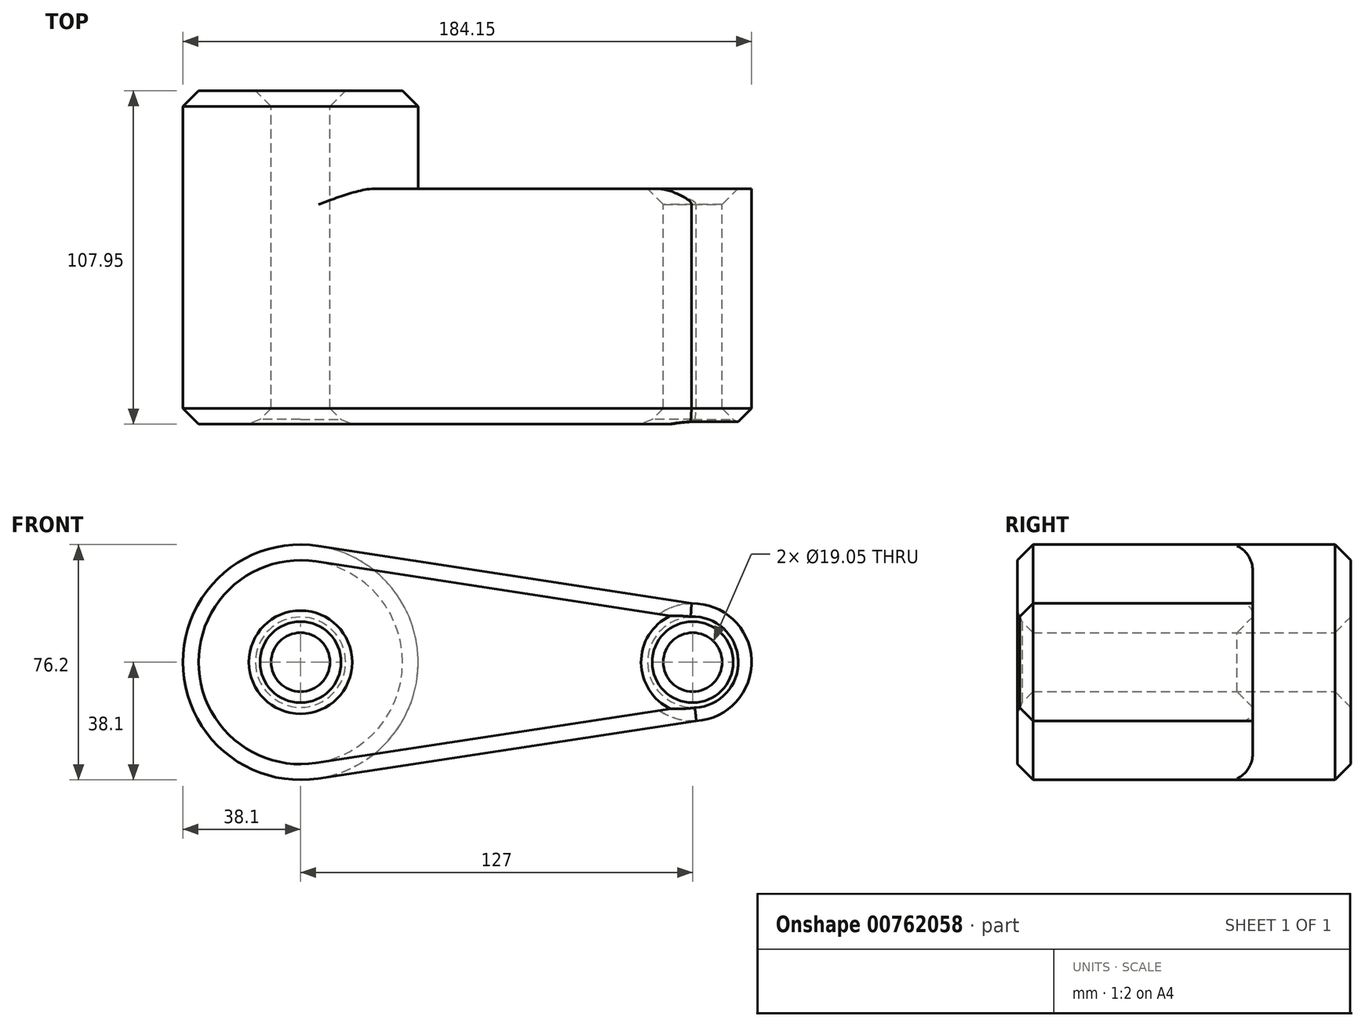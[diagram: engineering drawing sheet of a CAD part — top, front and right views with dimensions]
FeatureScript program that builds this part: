
annotation { "Feature Type Name" : "Feature", "Feature Type Description" : "" }
export const myFeature = defineFeature(function(context is Context, id is Id, definition is map)
    precondition{}
    {
        {
            var Q0;
            Q0=qCreatedBy(makeId("Front.planeOp"),FACE);
            var sketch = newSketch(context, id + "F0", { "sketchPlane" : qUnion([Q0])});
            skCircle(sketch, "E0", {"center": v(0, 0) * mm, "radius": 38.1 * mm});
            skCircle(sketch, "E1", {"center": v(127, 0) * mm, "radius": 19.05 * mm});
            skLineSegment(sketch, "E2", {"start": v(5.8, 37.66) * mm, "end": v(126.63, 19.05) * mm});
            skLineSegment(sketch, "E3", {"start": v(5.74, -37.67) * mm, "end": v(131.55, -18.5) * mm});
            skCircle(sketch, "E4", {"center": v(0, 0) * mm, "radius": 9.53 * mm});
            skCircle(sketch, "E5", {"center": v(127, 0) * mm, "radius": 9.53 * mm});
            skSolve(sketch);
        }
        {
            var Q0;
            Q0 = qSketchRegion(id + "F0", true);
            extrude(context, id + "F1", {"entities" : qUnion([Q0]), "depth" : 76.2 * mm, "offsetDistance" : 25.4 * mm});
        }
        {
            var Q0;
            Q0=makeQuery(id+"F0.imprint","IMPRINT",FACE,{"disambiguationData":[TD([[makeQuery(id+"F0.imprint","IMPRINT",EDGE,{"derivedFrom":sQuery(id+"F0.wireOp",EDGE,"E4")}),-1.0]])]});
            extrude(context, id + "F2", {"entities" : qUnion([Q0]), "operationType" : NewBodyOperationType.ADD, "oppositeDirection" : true, "depth" : 31.75 * mm, "offsetDistance" : 25.4 * mm});
        }
        {
            var Q0;
            Q0=makeQuery(id+"F2.opExtrude","CAP_EDGE",EDGE,{"disambiguationData":[OSD([sQuery(id+"F0.wireOp",EDGE,"E4")])],"isStart":false});
            chamfer(context, id + "F3", {"entities" : qUnion([Q0]), "chamferType" : ChamferType.OFFSET_ANGLE, "width" : 5.08 * mm, "oppositeDirection" : false, "angle" : 45 * degree, "tangentPropagation" : true});
        }
        {
            var Q0;
            Q0=makeQuery(id+"F2.opExtrude","CAP_EDGE",EDGE,{"disambiguationData":[OSD([sQuery(id+"F0.wireOp",EDGE,"E0")])],"isStart":false});
            chamfer(context, id + "F4", {"entities" : qUnion([Q0]), "width" : 5.08 * mm, "tangentPropagation" : true});
        }
        {
            var Q0;
            Q0=makeQuery(id+"F1.opExtrude","CAP_EDGE",EDGE,{"disambiguationData":[OSD([sQuery(id+"F0.wireOp",EDGE,"E5")])],"isStart":true});
            chamfer(context, id + "F5", {"entities" : qUnion([Q0]), "width" : 5.08 * mm, "tangentPropagation" : true});
        }
        {
            var Q0;
            Q0=makeQuery(id+"F1.opExtrude","CAP_EDGE",EDGE,{"disambiguationData":[OSD([sQuery(id+"F0.wireOp",EDGE,"E4")])],"isStart":false});
            var Q1;
            Q1=makeQuery(id+"F1.opExtrude","CAP_EDGE",EDGE,{"disambiguationData":[OSD([sQuery(id+"F0.wireOp",EDGE,"E5")])],"isStart":false});
            chamfer(context, id + "F6", {"entities" : qUnion([Q0, Q1]), "width" : 5.08 * mm, "tangentPropagation" : true});
        }
        {
            var Q0;
            Q0=makeQuery(id+"F1.opExtrude","CAP_FACE",FACE,{"disambiguationData":[OSD([sQuery(id+"F0.wireOp",EDGE,"E0"),sQuery(id+"F0.wireOp",EDGE,"E1"),sQuery(id+"F0.wireOp",EDGE,"E2"),sQuery(id+"F0.wireOp",EDGE,"E3"),sQuery(id+"F0.wireOp",EDGE,"E4"),sQuery(id+"F0.wireOp",EDGE,"E5")])],"isStart":false});
            chamfer(context, id + "F7", {"entities" : qUnion([Q0]), "width" : 5.08 * mm, "tangentPropagation" : true});
        }
        {
            var Q0;
            Q0=makeQuery(id+"F1.opExtrude","CAP_EDGE",EDGE,{"disambiguationData":[OSD([sQuery(id+"F0.wireOp",EDGE,"E3")])],"isStart":true});
            fillet(context, id + "F8", {"entities" : qUnion([Q0]), "radius" : 5.08 * mm, "tangentPropagation" : true, "allowEdgeOverflow" : false});
        }
        {
            var Q0;
            Q0=makeQuery(id+"F1.opExtrude","CAP_EDGE",EDGE,{"disambiguationData":[OSD([sQuery(id+"F0.wireOp",EDGE,"E2")])],"isStart":true});
            fillet(context, id + "F9", {"entities" : qUnion([Q0]), "radius" : 5.08 * mm, "tangentPropagation" : true, "allowEdgeOverflow" : false});
        }
    });
